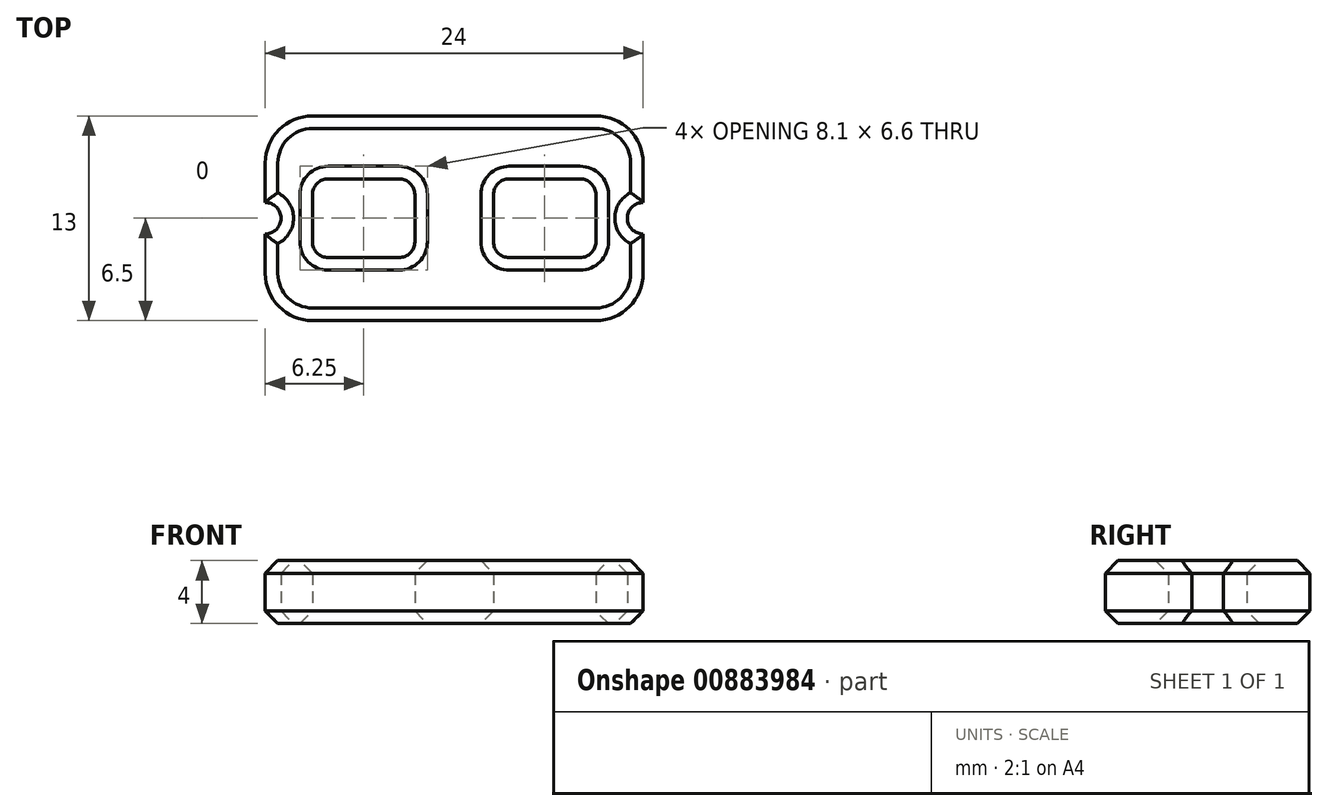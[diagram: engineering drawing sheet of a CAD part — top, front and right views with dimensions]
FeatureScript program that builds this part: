
annotation { "Feature Type Name" : "Feature", "Feature Type Description" : "" }
export const myFeature = defineFeature(function(context is Context, id is Id, definition is map)
    precondition{}
    {
        {
            var Q0;
            Q0=qCreatedBy(makeId("Top.planeOp"),FACE);
            var sketch = newSketch(context, id + "F0", { "sketchPlane" : qUnion([Q0])});
            skLineSegment(sketch, "E0.bottom", {"start": v(-9, 6.5) * mm, "end": v(9, 6.5) * mm});
            skLineSegment(sketch, "E0.top", {"start": v(-9, -6.5) * mm, "end": v(9, -6.5) * mm});
            skLineSegment(sketch, "E0.left", {"start": v(-12, 3.5) * mm, "end": v(-12, 1) * mm});
            skLineSegment(sketch, "E1", {"start": v(-12, -6.5) * mm, "end": v(12, 6.5) * mm, "construction": true});
            skLineSegment(sketch, "E2.bottom", {"start": v(-8, 2.5) * mm, "end": v(-3.5, 2.5) * mm});
            skLineSegment(sketch, "E2.top", {"start": v(-8, -2.5) * mm, "end": v(-3.5, -2.5) * mm});
            skLineSegment(sketch, "E2.left", {"start": v(-9, 1.5) * mm, "end": v(-9, -1.5) * mm});
            skLineSegment(sketch, "E2.right", {"start": v(-2.5, 1.5) * mm, "end": v(-2.5, -1.5) * mm});
            skPoint(sketch, "E3.visualSharp", {"position": v(-12, 6.5) * mm});
            skArc(sketch, "E3.filletArc", {"start": v(-9, 6.5) * mm, "mid": v(-11.12, 5.62) * mm, "end": v(-12, 3.5) * mm});
            skPoint(sketch, "E4.visualSharp", {"position": v(-12, -6.5) * mm});
            skArc(sketch, "E4.filletArc", {"start": v(-12, -3.5) * mm, "mid": v(-11.12, -5.62) * mm, "end": v(-9, -6.5) * mm});
            skPoint(sketch, "E5.visualSharp", {"position": v(-9, 2.5) * mm});
            skArc(sketch, "E5.filletArc", {"start": v(-8, 2.5) * mm, "mid": v(-8.7, 2.2) * mm, "end": v(-9, 1.5) * mm});
            skPoint(sketch, "E6.visualSharp", {"position": v(-9, -2.5) * mm});
            skArc(sketch, "E6.filletArc", {"start": v(-9, -1.5) * mm, "mid": v(-8.7, -2.2) * mm, "end": v(-8, -2.5) * mm});
            skPoint(sketch, "E7.visualSharp", {"position": v(-2.5, -2.5) * mm});
            skArc(sketch, "E7.filletArc", {"start": v(-3.5, -2.5) * mm, "mid": v(-2.8, -2.2) * mm, "end": v(-2.5, -1.5) * mm});
            skPoint(sketch, "E8.visualSharp", {"position": v(-2.5, 2.5) * mm});
            skArc(sketch, "E8.filletArc", {"start": v(-2.5, 1.5) * mm, "mid": v(-2.8, 2.2) * mm, "end": v(-3.5, 2.5) * mm});
            skArc(sketch, "E9.MirrorCS", {"start": v(3.5, -2.5) * mm, "mid": v(2.8, -2.2) * mm, "end": v(2.5, -1.5) * mm});
            skArc(sketch, "E10.MirrorCS", {"start": v(9, -1.5) * mm, "mid": v(8.7, -2.2) * mm, "end": v(8, -2.5) * mm});
            skArc(sketch, "E11.MirrorCS", {"start": v(8, 2.5) * mm, "mid": v(8.7, 2.2) * mm, "end": v(9, 1.5) * mm});
            skPoint(sketch, "E12.MirrorP", {"position": v(2.5, 2.5) * mm});
            skArc(sketch, "E13.MirrorCS", {"start": v(2.5, 1.5) * mm, "mid": v(2.8, 2.2) * mm, "end": v(3.5, 2.5) * mm});
            skLineSegment(sketch, "E14.MirrorCS", {"start": v(8, 2.5) * mm, "end": v(3.5, 2.5) * mm});
            skPoint(sketch, "E15.MirrorP", {"position": v(9, -2.5) * mm});
            skLineSegment(sketch, "E16.MirrorCS", {"start": v(8, -2.5) * mm, "end": v(3.5, -2.5) * mm});
            skLineSegment(sketch, "E17.MirrorCS", {"start": v(9, 1.5) * mm, "end": v(9, -1.5) * mm});
            skPoint(sketch, "E18.MirrorP", {"position": v(9, 2.5) * mm});
            skLineSegment(sketch, "E19.MirrorCS", {"start": v(2.5, 1.5) * mm, "end": v(2.5, -1.5) * mm});
            skPoint(sketch, "E20.MirrorP", {"position": v(2.5, -2.5) * mm});
            skPoint(sketch, "E21.visualSharp", {"position": v(12, 6.5) * mm});
            skArc(sketch, "E21.filletArc", {"start": v(12, 3.5) * mm, "mid": v(11.12, 5.62) * mm, "end": v(9, 6.5) * mm});
            skPoint(sketch, "E22.visualSharp", {"position": v(12, -6.5) * mm});
            skArc(sketch, "E22.filletArc", {"start": v(9, -6.5) * mm, "mid": v(11.12, -5.62) * mm, "end": v(12, -3.5) * mm});
            skArc(sketch, "E23", {"start": v(-12, -1) * mm, "mid": v(-11, 0) * mm, "end": v(-12, 1) * mm});
            skLineSegment(sketch, "E24.trimOffspring", {"start": v(-12, -1) * mm, "end": v(-12, -3.5) * mm});
            skPoint(sketch, "E25.visualSharp", {"position": v(-12, 1) * mm});
            skLineSegment(sketch, "E25.filletArc", {"start": v(-12, 1) * mm, "end": v(-12, 1) * mm});
            skPoint(sketch, "E26.visualSharp", {"position": v(-12, -1) * mm});
            skLineSegment(sketch, "E26.filletArc", {"start": v(-12, -1) * mm, "end": v(-12, -1) * mm});
            skLineSegment(sketch, "E27.MirrorCS", {"start": v(12, 3.5) * mm, "end": v(12, 1) * mm});
            skLineSegment(sketch, "E28.MirrorCS", {"start": v(12, -1) * mm, "end": v(12, -3.5) * mm});
            skLineSegment(sketch, "E29.MirrorCS", {"start": v(12, 1) * mm, "end": v(12, 1) * mm});
            skLineSegment(sketch, "E30.MirrorCS", {"start": v(12, -1) * mm, "end": v(12, -1) * mm});
            skArc(sketch, "E31.MirrorCS", {"start": v(12, -1) * mm, "mid": v(11, 0) * mm, "end": v(12, 1) * mm});
            skSolve(sketch);
        }
        {
            var Q0;
            Q0 = qSketchRegion(id + "F0", true);
            extrude(context, id + "F1", {"entities" : qUnion([Q0]), "depth" : 4 * mm, "offsetDistance" : 25 * mm});
        }
        {
            var Q0;
            Q0=makeQuery(id+"F1.opExtrude","CAP_FACE",FACE,{"disambiguationData":[OSD([sQuery(id+"F0.wireOp",EDGE,"E0.bottom"),sQuery(id+"F0.wireOp",EDGE,"E0.top"),sQuery(id+"F0.wireOp",EDGE,"E0.left"),sQuery(id+"F0.wireOp",EDGE,"E2.bottom"),sQuery(id+"F0.wireOp",EDGE,"E2.top"),sQuery(id+"F0.wireOp",EDGE,"E2.left"),sQuery(id+"F0.wireOp",EDGE,"E2.right"),sQuery(id+"F0.wireOp",EDGE,"E3.filletArc"),sQuery(id+"F0.wireOp",EDGE,"E4.filletArc"),sQuery(id+"F0.wireOp",EDGE,"E5.filletArc"),sQuery(id+"F0.wireOp",EDGE,"E6.filletArc"),sQuery(id+"F0.wireOp",EDGE,"E7.filletArc"),sQuery(id+"F0.wireOp",EDGE,"E8.filletArc"),sQuery(id+"F0.wireOp",EDGE,"E9.MirrorCS"),sQuery(id+"F0.wireOp",EDGE,"E10.MirrorCS"),sQuery(id+"F0.wireOp",EDGE,"E11.MirrorCS"),sQuery(id+"F0.wireOp",EDGE,"E13.MirrorCS"),sQuery(id+"F0.wireOp",EDGE,"E14.MirrorCS"),sQuery(id+"F0.wireOp",EDGE,"E16.MirrorCS"),sQuery(id+"F0.wireOp",EDGE,"E17.MirrorCS"),sQuery(id+"F0.wireOp",EDGE,"E19.MirrorCS"),sQuery(id+"F0.wireOp",EDGE,"E21.filletArc"),sQuery(id+"F0.wireOp",EDGE,"E22.filletArc"),sQuery(id+"F0.wireOp",EDGE,"E23"),sQuery(id+"F0.wireOp",EDGE,"E24.trimOffspring"),sQuery(id+"F0.wireOp",EDGE,"E27.MirrorCS"),sQuery(id+"F0.wireOp",EDGE,"E28.MirrorCS"),sQuery(id+"F0.wireOp",EDGE,"E31.MirrorCS")])],"isStart":false});
            var Q1;
            Q1=makeQuery(id+"F1.opExtrude","CAP_FACE",FACE,{"disambiguationData":[OSD([sQuery(id+"F0.wireOp",EDGE,"E0.bottom"),sQuery(id+"F0.wireOp",EDGE,"E0.top"),sQuery(id+"F0.wireOp",EDGE,"E0.left"),sQuery(id+"F0.wireOp",EDGE,"E2.bottom"),sQuery(id+"F0.wireOp",EDGE,"E2.top"),sQuery(id+"F0.wireOp",EDGE,"E2.left"),sQuery(id+"F0.wireOp",EDGE,"E2.right"),sQuery(id+"F0.wireOp",EDGE,"E3.filletArc"),sQuery(id+"F0.wireOp",EDGE,"E4.filletArc"),sQuery(id+"F0.wireOp",EDGE,"E5.filletArc"),sQuery(id+"F0.wireOp",EDGE,"E6.filletArc"),sQuery(id+"F0.wireOp",EDGE,"E7.filletArc"),sQuery(id+"F0.wireOp",EDGE,"E8.filletArc"),sQuery(id+"F0.wireOp",EDGE,"E9.MirrorCS"),sQuery(id+"F0.wireOp",EDGE,"E10.MirrorCS"),sQuery(id+"F0.wireOp",EDGE,"E11.MirrorCS"),sQuery(id+"F0.wireOp",EDGE,"E13.MirrorCS"),sQuery(id+"F0.wireOp",EDGE,"E14.MirrorCS"),sQuery(id+"F0.wireOp",EDGE,"E16.MirrorCS"),sQuery(id+"F0.wireOp",EDGE,"E17.MirrorCS"),sQuery(id+"F0.wireOp",EDGE,"E19.MirrorCS"),sQuery(id+"F0.wireOp",EDGE,"E21.filletArc"),sQuery(id+"F0.wireOp",EDGE,"E22.filletArc"),sQuery(id+"F0.wireOp",EDGE,"E23"),sQuery(id+"F0.wireOp",EDGE,"E24.trimOffspring"),sQuery(id+"F0.wireOp",EDGE,"E27.MirrorCS"),sQuery(id+"F0.wireOp",EDGE,"E28.MirrorCS"),sQuery(id+"F0.wireOp",EDGE,"E31.MirrorCS")])],"isStart":true});
            chamfer(context, id + "F2", {"entities" : qUnion([Q0, Q1]), "width" : .8 * mm, "tangentPropagation" : true});
        }
    });
